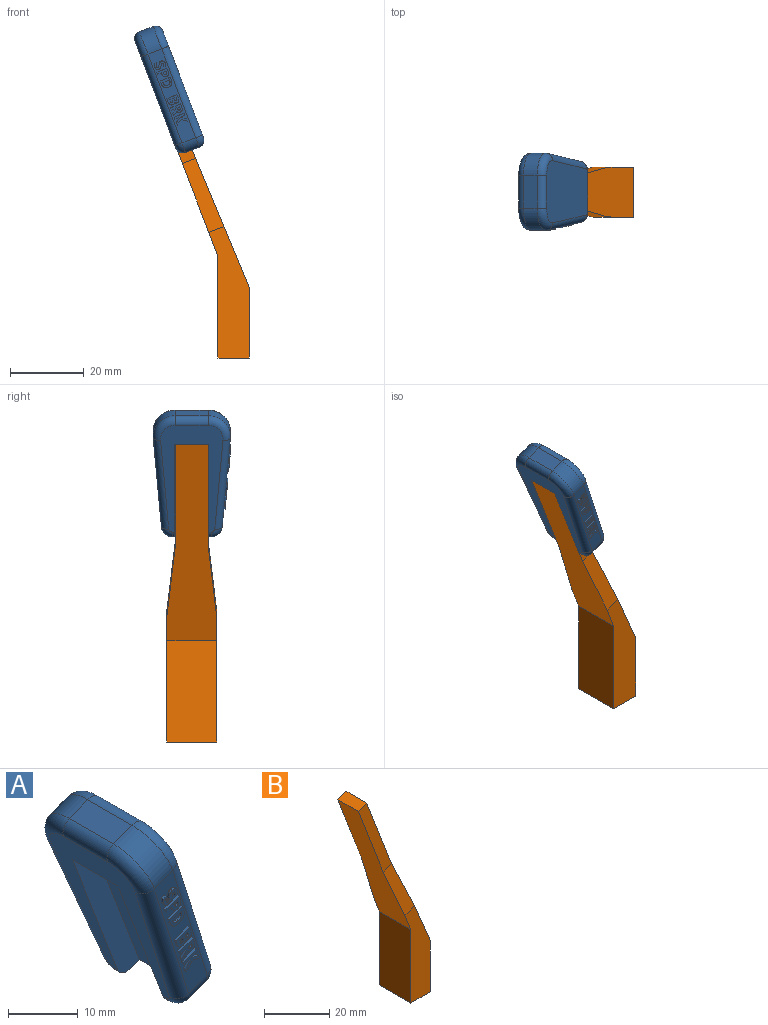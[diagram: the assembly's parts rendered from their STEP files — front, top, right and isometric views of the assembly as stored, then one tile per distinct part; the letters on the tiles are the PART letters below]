
ASSEMBLY  parts=2 mates=1
PART A: 155 faces, bbox 19.4x21.9x34.7 mm
  f0: plane 25.48x12.91mm, normal (0.03,-1,-0.08), area 75.9mm2, adj f7,f10,f12,f21,f31,f32,f33,f34
  f1: plane 28.96x16.93mm, normal (-0.93,0,-0.36), area 221.2mm2, adj f2,f19,f20,f21,f22,f23,f24,f25
  f2: cylinder r=2mm len=2.58mm, axis (0,-1,0), area 2mm2, adj f1,f4,f23,f27
  f3: plane 25.48x12.91mm, normal (0.03,1,-0.08), area 103.4mm2, adj f8,f9,f17,f24
  f4: plane 10.49x3.74mm, normal (0.36,0,-0.93), area 23.6mm2, adj f2,f9,f10,f16,f25,f27,f29,f30
  f5: plane 8.93x3.74mm, normal (-0.36,0,0.93), area 35.7mm2, adj f7,f8,f13,f20
  f6: plane 28.96x16.93mm, normal (0.93,0,0.36), area 455.8mm2, adj f11,f12,f13,f14,f15,f16,f17,f18
  f7: cylinder r=6mm len=7.51mm, axis (-0.93,0,-0.36), area 39.8mm2, adj f0,f5,f11,f19
  f8: cylinder r=6mm len=7.51mm, axis (0.93,0,0.36), area 39.8mm2, adj f3,f5,f15,f22
  f9: cylinder r=3mm len=4.72mm, axis (-0.93,0,-0.36), area 17.8mm2, adj f3,f4,f18,f26
  f10: cylinder r=3mm len=4.72mm, axis (0.93,0,0.36), area 17.8mm2, adj f0,f4,f14,f23
  f11: torus R=4mm, axis (-0.93,0,-0.36), area 27.4mm2, adj f6,f7,f12,f13
  f12: cylinder r=2mm len=24.93mm, axis (0.36,0.09,-0.93), area 81.2mm2, adj f0,f6,f11,f14
  f13: cylinder r=2mm len=8.93mm, axis (0,-1,0), area 28mm2, adj f5,f6,f11,f15
  f14: torus R=1mm, axis (-0.93,0,-0.36), area 10.6mm2, adj f6,f10,f12,f16
  f15: torus R=4mm, axis (-0.93,0,-0.36), area 27.4mm2, adj f6,f8,f13,f17
  f16: cylinder r=2mm len=10.49mm, axis (0,1,0), area 33mm2, adj f4,f6,f14,f18
  f17: cylinder r=2mm len=24.93mm, axis (-0.36,0.09,0.93), area 81.2mm2, adj f3,f6,f15,f18
  f18: torus R=1mm, axis (-0.93,0,-0.36), area 10.6mm2, adj f6,f9,f16,f17
  f19: torus R=4mm, axis (-0.93,0,-0.36), area 27.4mm2, adj f1,f7,f20,f21
  f20: cylinder r=2mm len=8.93mm, axis (0,1,0), area 28mm2, adj f1,f5,f19,f22
  f21: cylinder r=2mm len=24.62mm, axis (-0.36,-0.09,0.93), area 81.2mm2, adj f0,f1,f19,f23
  f22: torus R=4mm, axis (-0.93,0,-0.36), area 27.4mm2, adj f1,f8,f20,f24
  f23: torus R=1mm, axis (-0.93,0,-0.36), area 10.6mm2, adj f1,f2,f10,f21
  f24: cylinder r=2mm len=24.62mm, axis (0.36,-0.09,-0.93), area 81.2mm2, adj f1,f3,f22,f26
  f25: cylinder r=2mm len=2.58mm, axis (0,-1,0), area 2mm2, adj f1,f4,f26,f29
  f26: torus R=1mm, axis (-0.93,0,-0.36), area 10.6mm2, adj f1,f9,f24,f25
  f27: plane 26.54x13.54mm, normal (0,1,0), area 109.1mm2, adj f1,f2,f4,f28,f30
  f28: plane 9.2x3.74mm, normal (0.36,0,-0.93), area 36.8mm2, adj f1,f27,f29,f30
  f29: plane 26.54x13.54mm, normal (0,-1,0), area 109.1mm2, adj f1,f4,f25,f28,f30
  f30: plane 25.69x9.8mm, normal (-0.93,0,-0.36), area 253mm2, adj f4,f27,f28,f29
  f31: extruded ~0.69x0.42mm, area 0.3mm2, adj f0,f32,f58,f59
  f32: extruded ~0.41x0.41mm, area 0.2mm2, adj f0,f31,f33,f59
  f33: extruded ~0.69x0.45mm, area 0.3mm2, adj f0,f32,f34,f59
  f34: extruded ~0.47x0.43mm, area 0.2mm2, adj f0,f33,f35,f59
  f35: extruded ~0.41x0.19mm, area 0.1mm2, adj f0,f34,f36,f59
  f36: extruded ~0.4x0.13mm, area 0.1mm2, adj f0,f35,f37,f59
  f37: extruded ~0.41x0.24mm, area 0.1mm2, adj f0,f36,f38,f59
  f38: extruded ~0.42x0.25mm, area 0.1mm2, adj f0,f37,f39,f59
  f39: extruded ~0.42x0.32mm, area 0.1mm2, adj f0,f38,f40,f59
  f40: extruded ~0.44x0.43mm, area 0.2mm2, adj f0,f39,f41,f59
  f41: plane 0.53x0.42mm, normal (-0.03,0.08,-1), area 0.2mm2, adj f0,f40,f42,f59
  f42: extruded ~0.48x0.44mm, area 0.2mm2, adj f0,f41,f43,f59
  f43: extruded ~0.45x0.44mm, area 0.2mm2, adj f0,f42,f44,f59
  f44: extruded ~0.62x0.47mm, area 0.3mm2, adj f0,f43,f45,f59
  f45: extruded ~0.67x0.42mm, area 0.3mm2, adj f0,f44,f46,f59
  f46: extruded ~0.41x0.32mm, area 0.1mm2, adj f0,f45,f47,f59
  f47: extruded ~0.42x0.32mm, area 0.1mm2, adj f0,f46,f48,f59
  f48: extruded ~0.49x0.43mm, area 0.2mm2, adj f0,f47,f49,f59
  f49: extruded ~0.45x0.43mm, area 0.2mm2, adj f0,f48,f50,f59
  f50: extruded ~0.41x0.21mm, area 0.1mm2, adj f0,f49,f51,f59
  f51: extruded ~0.4x0.14mm, area 0.1mm2, adj f0,f50,f52,f59
  f52: extruded ~0.41x0.27mm, area 0.1mm2, adj f0,f51,f53,f59
  f53: extruded ~0.43x0.29mm, area 0.1mm2, adj f0,f52,f54,f59
  f54: extruded ~0.43x0.4mm, area 0.2mm2, adj f0,f53,f55,f59
  f55: extruded ~0.56x0.44mm, area 0.2mm2, adj f0,f54,f56,f59
  f56: plane 0.55x0.4mm, normal (-0.36,-0.09,0.93), area 0.2mm2, adj f0,f55,f57,f59
  f57: extruded ~0.86x0.47mm, area 0.3mm2, adj f0,f56,f58,f59
  f58: extruded ~0.68x0.5mm, area 0.3mm2, adj f0,f31,f57,f59
  f59: plane 3.13x2.37mm, normal (0.03,-1,-0.08), area 3.2mm2, adj f31,f32,f33,f34,f35,f36,f37,f38
  f60: extruded ~0.78x0.42mm, area 0.3mm2, adj f0,f61,f75,f76
  f61: extruded ~0.55x0.53mm, area 0.3mm2, adj f0,f60,f62,f76
  f62: extruded ~0.86x0.47mm, area 0.3mm2, adj f0,f61,f63,f76
  f63: plane 0.89x0.48mm, normal (0.93,0,0.36), area 0.4mm2, adj f0,f62,f64,f76
  f64: plane 2.72x1.06mm, normal (-0.36,-0.09,0.93), area 1.2mm2, adj f0,f63,f65,f76
  f65: plane 0.6x0.45mm, normal (-0.93,0,-0.36), area 0.2mm2, adj f0,f64,f66,f76
  f66: plane 0.98x0.4mm, normal (0.36,0.09,-0.93), area 0.4mm2, adj f0,f65,f67,f76
  f67: plane 0.42x0.28mm, normal (-0.93,0,-0.36), area 0.1mm2, adj f0,f66,f75,f76
  f68: plane 0.42x0.22mm, normal (0.93,0,0.36), area 0.1mm2, adj f69,f74,f76,f77
  f69: plane 0.82x0.4mm, normal (0.36,0.09,-0.93), area 0.3mm2, adj f68,f70,f76,f77
  f70: plane 0.42x0.29mm, normal (-0.93,0,-0.36), area 0.1mm2, adj f69,f71,f76,f77
  f71: extruded ~0.43x0.41mm, area 0.2mm2, adj f70,f72,f76,f77
  f72: extruded ~0.41x0.27mm, area 0.1mm2, adj f71,f73,f76,f77
  f73: extruded ~0.41x0.37mm, area 0.1mm2, adj f72,f74,f76,f77
  f74: extruded ~0.43x0.39mm, area 0.2mm2, adj f68,f73,f76,f77
  f75: extruded ~0.72x0.54mm, area 0.4mm2, adj f0,f60,f67,f76
  f76: plane 3.18x2.3mm, normal (0.03,-1,-0.08), area 3.4mm2, adj f60,f61,f62,f63,f64,f65,f66,f67
  f77: plane 0.97x0.91mm, normal (0.03,-1,-0.08), area 0.6mm2, adj f68,f69,f70,f71,f72,f73,f74
  f78: extruded ~1.13x0.67mm, area 0.6mm2, adj f79,f89,f90,f91
  f79: extruded ~1.22x0.62mm, area 0.6mm2, adj f78,f80,f90,f91
  f80: plane 0.42x0.28mm, normal (0.93,0,0.36), area 0.1mm2, adj f79,f81,f90,f91
  f81: plane 1.77x0.7mm, normal (0.36,0.09,-0.93), area 0.8mm2, adj f80,f89,f90,f91
  f82: extruded ~1.18x0.43mm, area 0.5mm2, adj f0,f83,f88,f90
  f83: extruded ~0.85x0.77mm, area 0.5mm2, adj f0,f82,f84,f90
  f84: extruded ~1.19x0.49mm, area 0.5mm2, adj f0,f83,f85,f90
  f85: plane 0.88x0.48mm, normal (0.93,0,0.36), area 0.4mm2, adj f0,f84,f86,f90
  f86: plane 2.72x1.06mm, normal (-0.36,-0.09,0.93), area 1.2mm2, adj f0,f85,f87,f90
  f87: plane 0.8x0.47mm, normal (-0.93,0,-0.36), area 0.3mm2, adj f0,f86,f88,f90
  f88: extruded ~0.99x0.79mm, area 0.5mm2, adj f0,f82,f87,f90
  f89: plane 0.43x0.34mm, normal (-0.93,0,-0.36), area 0.1mm2, adj f78,f81,f90,f91
  f90: plane 3.21x2.92mm, normal (0.03,-1,-0.08), area 4.3mm2, adj f78,f79,f80,f81,f82,f83,f84,f85
  f91: plane 2.07x1.62mm, normal (0.03,-1,-0.08), area 1.9mm2, adj f78,f79,f80,f81,f89
  f92: plane 0.72x0.4mm, normal (0.36,0.09,-0.93), area 0.3mm2, adj f93,f116,f117,f118
  f93: plane 0.43x0.39mm, normal (-0.93,0,-0.36), area 0.2mm2, adj f92,f94,f117,f118
  f94: extruded ~0.64x0.44mm, area 0.3mm2, adj f93,f95,f117,f118
  f95: extruded ~0.41x0.33mm, area 0.1mm2, adj f94,f96,f117,f118
  f96: extruded ~0.43x0.35mm, area 0.2mm2, adj f95,f116,f117,f118
  f97: plane 0.43x0.36mm, normal (0.93,0,0.36), area 0.1mm2, adj f98,f114,f117,f119
  f98: plane 0.61x0.4mm, normal (0.36,0.09,-0.93), area 0.3mm2, adj f97,f99,f117,f119
  f99: plane 0.43x0.33mm, normal (-0.93,0,-0.36), area 0.1mm2, adj f98,f100,f117,f119
  f100: extruded ~0.43x0.42mm, area 0.2mm2, adj f99,f101,f117,f119
  f101: extruded ~0.41x0.23mm, area 0.1mm2, adj f100,f102,f117,f119
  f102: extruded ~0.41x0.29mm, area 0.1mm2, adj f101,f114,f117,f119
  f103: plane 0.87x0.48mm, normal (0.93,0,0.36), area 0.4mm2, adj f0,f104,f115,f117
  f104: plane 2.72x1.06mm, normal (-0.36,-0.09,0.93), area 1.2mm2, adj f0,f103,f105,f117
  f105: plane 1.04x0.49mm, normal (-0.93,0,-0.36), area 0.4mm2, adj f0,f104,f106,f117
  f106: extruded ~0.68x0.5mm, area 0.3mm2, adj f0,f105,f107,f117
  f107: extruded ~0.69x0.42mm, area 0.3mm2, adj f0,f106,f108,f117
  f108: extruded ~0.41x0.39mm, area 0.2mm2, adj f0,f107,f109,f117
  f109: extruded ~0.48x0.43mm, area 0.2mm2, adj f0,f108,f110,f117
  f110: plane 0.4x0.04mm, normal (0.36,0.09,-0.93), area 0mm2, adj f0,f109,f111,f117
  f111: extruded ~0.43x0.31mm, area 0.2mm2, adj f0,f110,f112,f117
  f112: extruded ~0.45x0.41mm, area 0.2mm2, adj f0,f111,f113,f117
  f113: extruded ~0.49x0.43mm, area 0.3mm2, adj f0,f112,f115,f117
  f114: extruded ~0.43x0.34mm, area 0.2mm2, adj f97,f102,f117,f119
  f115: extruded ~0.93x0.48mm, area 0.4mm2, adj f0,f103,f113,f117
  f116: plane 0.43x0.4mm, normal (0.93,0,0.36), area 0.2mm2, adj f92,f96,f117,f118
  f117: plane 3.23x2.82mm, normal (0.03,-1,-0.08), area 4.6mm2, adj f92,f93,f94,f95,f96,f97,f98,f99
  f118: plane 1.01x0.96mm, normal (0.03,-1,-0.08), area 0.6mm2, adj f92,f93,f94,f95,f96,f116
  f119: plane 0.93x0.81mm, normal (0.03,-1,-0.08), area 0.5mm2, adj f97,f98,f99,f100,f101,f102,f114
  f120: plane 1.05x0.43mm, normal (0.36,0.09,-0.93), area 0.4mm2, adj f0,f121,f138,f139
  f121: plane 0.43x0.34mm, normal (-0.93,0,-0.36), area 0.1mm2, adj f0,f120,f122,f139
  f122: plane 1.07x0.81mm, normal (-0.8,-0.07,0.6), area 0.5mm2, adj f0,f121,f123,f139
  f123: plane 0.67x0.46mm, normal (-0.93,0,-0.36), area 0.3mm2, adj f0,f122,f124,f139
  f124: extruded ~1.28x0.89mm, area 0.6mm2, adj f0,f123,f125,f139
  f125: extruded ~0.45x0.43mm, area 0.2mm2, adj f0,f124,f126,f139
  f126: extruded ~0.49x0.41mm, area 0.2mm2, adj f0,f125,f127,f139
  f127: extruded ~0.53x0.52mm, area 0.3mm2, adj f0,f126,f128,f139
  f128: extruded ~0.92x0.47mm, area 0.4mm2, adj f0,f127,f129,f139
  f129: plane 0.82x0.47mm, normal (0.93,0,0.36), area 0.3mm2, adj f0,f128,f130,f139
  f130: plane 2.72x1.06mm, normal (-0.36,-0.09,0.93), area 1.2mm2, adj f0,f129,f138,f139
  f131: plane 0.42x0.22mm, normal (0.93,0,0.36), area 0.1mm2, adj f132,f137,f139,f140
  f132: plane 0.74x0.4mm, normal (0.36,0.09,-0.93), area 0.3mm2, adj f131,f133,f139,f140
  f133: plane 0.41x0.21mm, normal (-0.93,0,-0.36), area 0.1mm2, adj f132,f134,f139,f140
  f134: extruded ~0.47x0.44mm, area 0.2mm2, adj f133,f135,f139,f140
  f135: extruded ~0.41x0.27mm, area 0.1mm2, adj f134,f136,f139,f140
  f136: extruded ~0.41x0.35mm, area 0.1mm2, adj f135,f137,f139,f140
  f137: extruded ~0.44x0.4mm, area 0.2mm2, adj f131,f136,f139,f140
  f138: plane 0.6x0.45mm, normal (-0.93,0,-0.36), area 0.2mm2, adj f0,f120,f130,f139
  f139: plane 3.19x3.18mm, normal (0.03,-1,-0.08), area 4.1mm2, adj f120,f121,f122,f123,f124,f125,f126,f127
  f140: plane 0.9x0.9mm, normal (0.03,-1,-0.08), area 0.5mm2, adj f131,f132,f133,f134,f135,f136,f137
  f141: plane 0.68x0.46mm, normal (-0.93,0,-0.36), area 0.3mm2, adj f0,f142,f153,f154
  f142: plane 1.56x1.16mm, normal (0.8,0.07,-0.6), area 0.8mm2, adj f0,f141,f143,f154
  f143: plane 1.57x0.52mm, normal (-0.3,0.07,-0.95), area 0.7mm2, adj f0,f142,f144,f154
  f144: plane 0.67x0.46mm, normal (0.93,0,0.36), area 0.3mm2, adj f0,f143,f145,f154
  f145: plane 1.21x0.47mm, normal (0.3,-0.07,0.95), area 0.5mm2, adj f0,f144,f146,f154
  f146: plane 0.42x0.42mm, normal (0.25,-0.07,0.97), area 0.2mm2, adj f0,f145,f147,f154
  f147: plane 1.25x0.5mm, normal (0.36,0.09,-0.93), area 0.5mm2, adj f0,f146,f148,f154
  f148: plane 0.6x0.45mm, normal (0.93,0,0.36), area 0.2mm2, adj f0,f147,f149,f154
  f149: plane 2.72x1.06mm, normal (-0.36,-0.09,0.93), area 1.2mm2, adj f0,f148,f150,f154
  f150: plane 0.6x0.45mm, normal (-0.93,0,-0.36), area 0.2mm2, adj f0,f149,f151,f154
  f151: plane 0.98x0.4mm, normal (0.36,0.09,-0.93), area 0.4mm2, adj f0,f150,f152,f154
  f152: plane 0.42x0.28mm, normal (-0.55,0.05,-0.83), area 0.1mm2, adj f0,f151,f153,f154
  f153: plane 1.17x0.88mm, normal (-0.79,-0.07,0.6), area 0.6mm2, adj f0,f141,f152,f154
  f154: plane 3.53x3.2mm, normal (0.03,-1,-0.08), area 3.8mm2, adj f141,f142,f143,f144,f145,f146,f147,f148
PART B: 18 faces, bbox 28.8x13.5x82.1 mm
  f0: plane 13.5x8.5mm, normal (0,0,-1), area 57mm2, adj f1,f2,f5,f6,f7,f8,f9,f10
  f1: plane 27.43x13.5mm, normal (-1,0,0), area 370.3mm2, adj f0,f4,f5,f6
  f2: plane 19.01x13.5mm, normal (1,0,0), area 256.7mm2, adj f0,f3,f5,f6
  f3: plane 35.05x14.56mm, normal (0.92,0,0.38), area 467.4mm2, adj f2,f5,f6,f12,f13,f14
  f4: plane 53.3x20.33mm, normal (-0.93,0,-0.36), area 590.1mm2, adj f1,f5,f6,f12,f13,f15,f16,f17
  f5: plane 35.59x11.01mm, normal (0,-1,0), area 254.4mm2, adj f0,f1,f2,f3,f4,f12
  f6: plane 35.59x11.01mm, normal (0,1,0), area 254.4mm2, adj f0,f1,f2,f3,f4,f13
  f7: plane 17x5.5mm, normal (0,-1,0), area 93.5mm2, adj f0,f8,f10,f11
  f8: plane 17x10.5mm, normal (-1,0,0), area 178.5mm2, adj f0,f7,f9,f11
  f9: plane 17x5.5mm, normal (0,1,0), area 93.5mm2, adj f0,f8,f10,f11
  f10: plane 17x10.5mm, normal (1,0,0), area 178.5mm2, adj f0,f7,f9,f11
  f11: plane 10.5x5.5mm, normal (0,0,-1), area 57.8mm2, adj f7,f8,f9,f10
  f12: plane 20.05x11.25mm, normal (-0.04,-0.99,0.1), area 83mm2, adj f3,f4,f5,f16
  f13: plane 20.05x11.25mm, normal (-0.04,0.99,0.1), area 83mm2, adj f3,f4,f6,f15
  f14: plane 28.03x10.69mm, normal (0.93,0,0.36), area 270mm2, adj f3,f15,f16,f17
  f15: plane 29.4x14.27mm, normal (0,1,0), area 114.9mm2, adj f4,f13,f14,f17
  f16: plane 29.4x14.27mm, normal (0,-1,0), area 114.9mm2, adj f4,f12,f14,f17
  f17: plane 9x3.58mm, normal (-0.36,0,0.93), area 34.5mm2, adj f4,f14,f15,f16
PLACE A t=(0.02,0,-0.53)mm
PLACE B at identity
MATE fastened A.f28 <-> B.f17  axis (0.36,0,-0.93) through (3.92,0,54.66)mm
